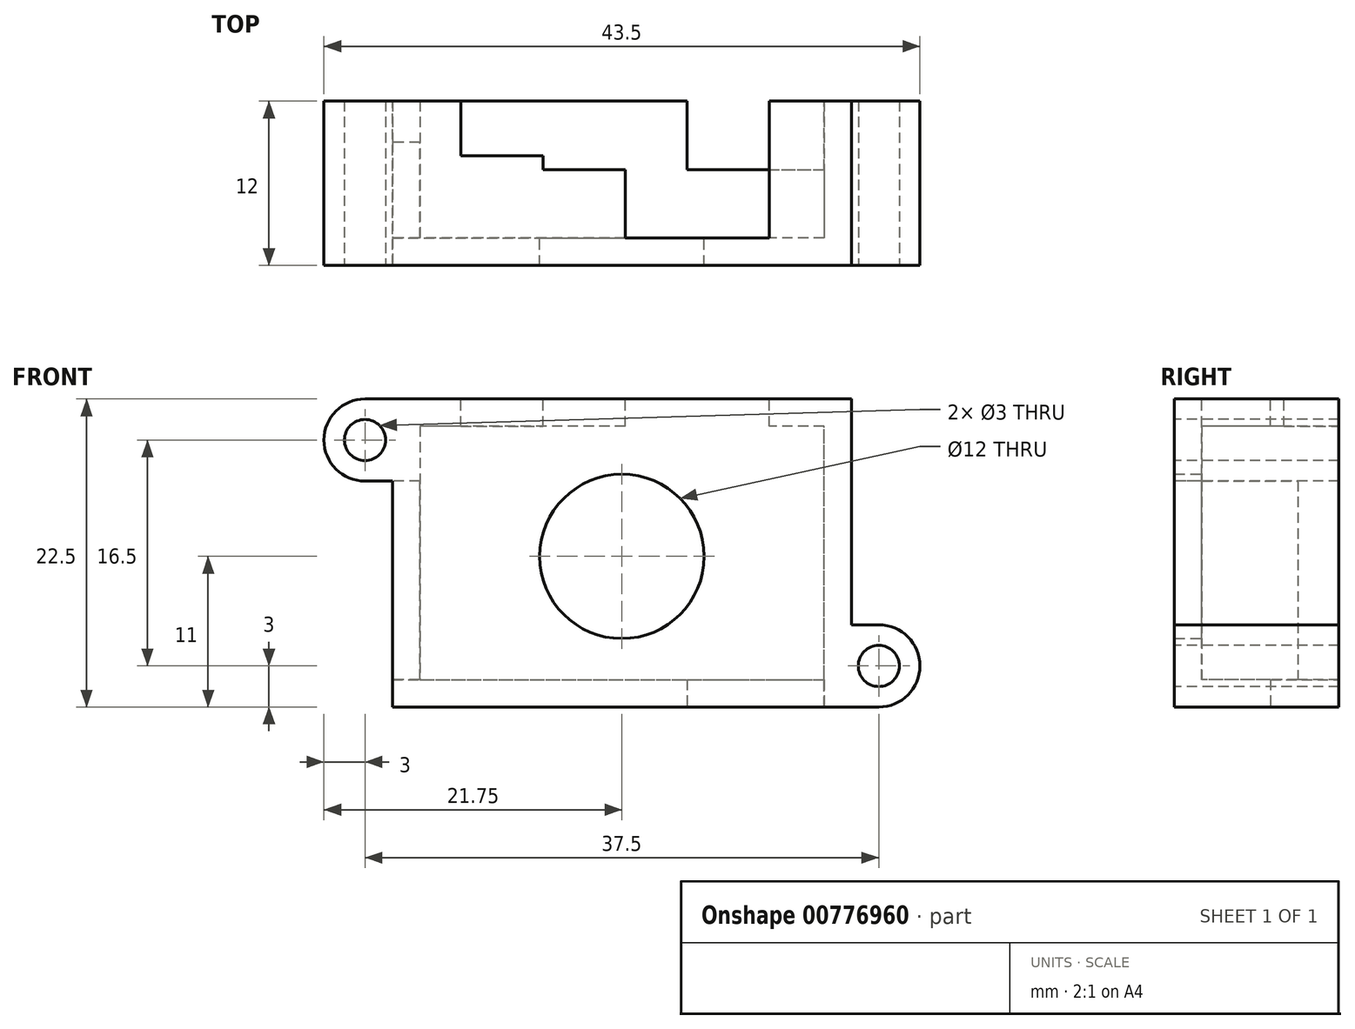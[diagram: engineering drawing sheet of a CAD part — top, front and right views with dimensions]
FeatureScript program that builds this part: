
annotation { "Feature Type Name" : "Feature", "Feature Type Description" : "" }
export const myFeature = defineFeature(function(context is Context, id is Id, definition is map)
    precondition{}
    {
        {
            var Q0;
            Q0=qCreatedBy(makeId("Front.planeOp"),FACE);
            var sketch = newSketch(context, id + "F0", { "sketchPlane" : qUnion([Q0])});
            skLineSegment(sketch, "E0.bottom", {"start": v(0, 0) * mm, "end": v(33.5, 0) * mm});
            skLineSegment(sketch, "E0.top", {"start": v(0, 22.5) * mm, "end": v(33.5, 22.5) * mm});
            skLineSegment(sketch, "E0.left", {"start": v(0, 0) * mm, "end": v(0, 22.5) * mm});
            skLineSegment(sketch, "E0.right", {"start": v(33.5, 0) * mm, "end": v(33.5, 22.5) * mm});
            skCircle(sketch, "E1", {"center": v(16.75, 11) * mm, "radius": 6 * mm});
            skSolve(sketch);
        }
        {
            var Q0;
            Q0=qSketchRegion(id+"F0",true);
            extrude(context, id + "F1", {"entities" : qUnion([Q0]), "depth" : 2 * mm, "offsetDistance" : 25 * mm});
        }
        {
            var Q0;
            Q0=makeQuery(id+"F1.opExtrude","CAP_FACE",FACE,{"disambiguationData":[OSD([sQuery(id+"F0.wireOp",EDGE,"E0.bottom"),sQuery(id+"F0.wireOp",EDGE,"E0.top"),sQuery(id+"F0.wireOp",EDGE,"E0.left"),sQuery(id+"F0.wireOp",EDGE,"E0.right"),sQuery(id+"F0.wireOp",EDGE,"E1")])],"isStart":true});
            var sketch = newSketch(context, id + "F2", { "sketchPlane" : qUnion([Q0])});
            skLineSegment(sketch, "E2", {"start": v(-33.5, 22.5) * mm, "end": v(-33.5, 0) * mm});
            skLineSegment(sketch, "E3", {"start": v(-33.5, 0) * mm, "end": v(0, 0) * mm});
            skLineSegment(sketch, "E4", {"start": v(0, 0) * mm, "end": v(0, 22.5) * mm});
            skLineSegment(sketch, "E5", {"start": v(0, 22.5) * mm, "end": v(-11, 22.5) * mm});
            skLineSegment(sketch, "E6", {"start": v(-11, 22.5) * mm, "end": v(-11, 20.5) * mm});
            skLineSegment(sketch, "E7", {"start": v(-11, 20.5) * mm, "end": v(-2, 20.5) * mm});
            skLineSegment(sketch, "E8", {"start": v(-2, 20.5) * mm, "end": v(-2, 2) * mm});
            skLineSegment(sketch, "E9", {"start": v(-2, 2) * mm, "end": v(-31.5, 2) * mm});
            skLineSegment(sketch, "E10", {"start": v(-31.5, 2) * mm, "end": v(-31.5, 20.5) * mm});
            skLineSegment(sketch, "E11", {"start": v(-31.5, 20.5) * mm, "end": v(-27.5, 20.5) * mm});
            skLineSegment(sketch, "E12", {"start": v(-27.5, 20.5) * mm, "end": v(-27.5, 22.5) * mm});
            skLineSegment(sketch, "E13", {"start": v(-27.5, 22.5) * mm, "end": v(-33.5, 22.5) * mm});
            skSolve(sketch);
        }
        {
            var Q0;
            Q0=qSketchRegion(id+"F2",true);
            extrude(context, id + "F3", {"entities" : qUnion([Q0]), "operationType" : NewBodyOperationType.ADD, "depth" : 10 * mm, "offsetDistance" : 25 * mm});
        }
        {
            var Q0;
            Q0=makeQuery(id+"F3.boolean.opBoolean","MERGE",FACE,{"derivedFrom":[makeQuery(id+"F1.opExtrude","SWEPT_FACE",FACE,{"disambiguationData":[OSD([sQuery(id+"F0.wireOp",EDGE,"E0.top")])]}),makeQuery(id+"F3.opExtrude","SWEPT_FACE",FACE,{"disambiguationData":[OSD([sQuery(id+"F2.wireOp",EDGE,"E5")])]}),makeQuery(id+"F3.opExtrude","SWEPT_FACE",FACE,{"disambiguationData":[OSD([sQuery(id+"F2.wireOp",EDGE,"E13")])]})]});
            var sketch = newSketch(context, id + "F4", { "sketchPlane" : qUnion([Q0])});
            skLineSegment(sketch, "E14.bottom", {"start": v(11, 10) * mm, "end": v(5, 10) * mm});
            skLineSegment(sketch, "E14.top", {"start": v(11, 6) * mm, "end": v(5, 6) * mm});
            skLineSegment(sketch, "E14.left", {"start": v(11, 10) * mm, "end": v(11, 6) * mm});
            skLineSegment(sketch, "E14.right", {"start": v(5, 10) * mm, "end": v(5, 6) * mm});
            skSolve(sketch);
        }
        {
            var Q0;
            Q0=qSketchRegion(id+"F4",true);
            var Q1;
            Q1=makeQuery(id+"F3.opExtrude","SWEPT_FACE",FACE,{"disambiguationData":[OSD([sQuery(id+"F2.wireOp",EDGE,"E7")])]});
            extrude(context, id + "F5", {"entities" : qUnion([Q0]), "operationType" : NewBodyOperationType.REMOVE, "endBound" : BoundingType.UP_TO_SURFACE, "oppositeDirection" : true, "depth" : 25 * mm, "endBoundEntityFace" : qUnion([Q1]), "offsetDistance" : 25 * mm});
        }
        {
            var Q0;
            Q0=makeQuery(id+"F1.opExtrude","CAP_FACE",FACE,{"disambiguationData":[OSD([sQuery(id+"F0.wireOp",EDGE,"E0.bottom"),sQuery(id+"F0.wireOp",EDGE,"E0.top"),sQuery(id+"F0.wireOp",EDGE,"E0.left"),sQuery(id+"F0.wireOp",EDGE,"E0.right"),sQuery(id+"F0.wireOp",EDGE,"E1")])],"isStart":false});
            var sketch = newSketch(context, id + "F6", { "sketchPlane" : qUnion([Q0])});
            skLineSegment(sketch, "E15.bottom", {"start": v(33.5, 0) * mm, "end": v(35.5, 0) * mm});
            skLineSegment(sketch, "E15.top", {"start": v(33.5, 6) * mm, "end": v(35.5, 6) * mm});
            skLineSegment(sketch, "E15.left", {"start": v(33.5, 0) * mm, "end": v(33.5, 6) * mm});
            skLineSegment(sketch, "E15.right", {"start": v(35.5, 0) * mm, "end": v(35.5, 6) * mm});
            skArc(sketch, "E16", {"start": v(35.5, 0) * mm, "mid": v(38.5, 3) * mm, "end": v(35.5, 6) * mm});
            skLineSegment(sketch, "E17.bottom", {"start": v(0, 22.5) * mm, "end": v(-2, 22.5) * mm});
            skLineSegment(sketch, "E17.top", {"start": v(0, 16.5) * mm, "end": v(-2, 16.5) * mm});
            skLineSegment(sketch, "E17.left", {"start": v(0, 22.5) * mm, "end": v(0, 16.5) * mm});
            skLineSegment(sketch, "E17.right", {"start": v(-2, 22.5) * mm, "end": v(-2, 16.5) * mm});
            skArc(sketch, "E18", {"start": v(-2, 22.5) * mm, "mid": v(-5, 19.5) * mm, "end": v(-2, 16.5) * mm});
            skCircle(sketch, "E19", {"center": v(35.5, 3) * mm, "radius": 1.5 * mm});
            skCircle(sketch, "E20", {"center": v(-2, 19.5) * mm, "radius": 1.5 * mm});
            skSolve(sketch);
        }
        {
            var Q0;
            Q0=qSketchRegion(id+"F6",true);
            var Q1;
            Q1=makeQuery(id+"F3.opExtrude","CAP_FACE",FACE,{"disambiguationData":[OSD([sQuery(id+"F2.wireOp",EDGE,"E2"),sQuery(id+"F2.wireOp",EDGE,"E3"),sQuery(id+"F2.wireOp",EDGE,"E4"),sQuery(id+"F2.wireOp",EDGE,"E5"),sQuery(id+"F2.wireOp",EDGE,"E6"),sQuery(id+"F2.wireOp",EDGE,"E7"),sQuery(id+"F2.wireOp",EDGE,"E8"),sQuery(id+"F2.wireOp",EDGE,"E9"),sQuery(id+"F2.wireOp",EDGE,"E10"),sQuery(id+"F2.wireOp",EDGE,"E11"),sQuery(id+"F2.wireOp",EDGE,"E12"),sQuery(id+"F2.wireOp",EDGE,"E13")])],"isStart":false});
            extrude(context, id + "F7", {"entities" : qUnion([Q0]), "operationType" : NewBodyOperationType.ADD, "endBound" : BoundingType.UP_TO_SURFACE, "oppositeDirection" : true, "depth" : 25 * mm, "endBoundEntityFace" : qUnion([Q1]), "offsetDistance" : 25 * mm});
        }
        {
            var Q0;
            Q0=makeQuery(id+"F7.boolean.opBoolean","MERGE",FACE,{"derivedFrom":[makeQuery(id+"F3.boolean.opBoolean","MERGE",FACE,{"derivedFrom":[makeQuery(id+"F1.opExtrude","SWEPT_FACE",FACE,{"disambiguationData":[OSD([sQuery(id+"F0.wireOp",EDGE,"E0.top")])]}),makeQuery(id+"F3.opExtrude","SWEPT_FACE",FACE,{"disambiguationData":[OSD([sQuery(id+"F2.wireOp",EDGE,"E5")])]}),makeQuery(id+"F3.opExtrude","SWEPT_FACE",FACE,{"disambiguationData":[OSD([sQuery(id+"F2.wireOp",EDGE,"E13")])]})]}),makeQuery(id+"F7.opExtrude","SWEPT_FACE",FACE,{"disambiguationData":[OSD([sQuery(id+"F6.wireOp",EDGE,"E17.bottom")])]})]});
            var sketch = newSketch(context, id + "F8", { "sketchPlane" : qUnion([Q0])});
            skLineSegment(sketch, "E21.bottom", {"start": v(11, 0) * mm, "end": v(17, 0) * mm});
            skLineSegment(sketch, "E21.top", {"start": v(11, 5) * mm, "end": v(17, 5) * mm});
            skLineSegment(sketch, "E21.left", {"start": v(11, 0) * mm, "end": v(11, 5) * mm});
            skLineSegment(sketch, "E21.right", {"start": v(17, 0) * mm, "end": v(17, 5) * mm});
            skSolve(sketch);
        }
        {
            var Q0;
            Q0=qSketchRegion(id+"F8",true);
            var Q1;
            Q1=makeQuery(id+"F3.opExtrude","SWEPT_FACE",FACE,{"disambiguationData":[OSD([sQuery(id+"F2.wireOp",EDGE,"E7")])]});
            extrude(context, id + "F9", {"entities" : qUnion([Q0]), "operationType" : NewBodyOperationType.ADD, "endBound" : BoundingType.UP_TO_SURFACE, "oppositeDirection" : true, "depth" : 25 * mm, "endBoundEntityFace" : qUnion([Q1]), "offsetDistance" : 25 * mm});
        }
        {
            var Q0;
            {var subQ0=sQuery(id+"F2.wireOp",EDGE,"E13");var subQ1=sQuery(id+"F2.wireOp",EDGE,"E12");var subQ2=sQuery(id+"F2.wireOp",EDGE,"E11");var subQ3=sQuery(id+"F2.wireOp",EDGE,"E10");var subQ4=sQuery(id+"F2.wireOp",EDGE,"E9");var subQ5=sQuery(id+"F2.wireOp",EDGE,"E8");var subQ6=sQuery(id+"F2.wireOp",EDGE,"E7");var subQ7=sQuery(id+"F2.wireOp",EDGE,"E6");var subQ8=sQuery(id+"F2.wireOp",EDGE,"E5");var subQ9=sQuery(id+"F2.wireOp",EDGE,"E4");var subQ10=sQuery(id+"F2.wireOp",EDGE,"E3");var subQ11=sQuery(id+"F2.wireOp",EDGE,"E2");Q0=makeQuery(id+"F7.boolean.opBoolean","MERGE",FACE,{"derivedFrom":[makeQuery(id+"F3.opExtrude","CAP_FACE",FACE,{"disambiguationData":[OSD([subQ11,subQ10,subQ9,subQ8,subQ7,subQ6,subQ5,subQ4,subQ3,subQ2,subQ1,subQ0])],"isStart":false}),makeQuery(id+"F7.opExtrude","CAP_FACE",FACE,{"disambiguationData":[OSD([subQ11,subQ10,subQ9,subQ8,subQ7,subQ6,subQ5,subQ4,subQ3,subQ2,subQ1,subQ0]),OD(0.0)],"isStart":false}),makeQuery(id+"F7.opExtrude","CAP_FACE",FACE,{"disambiguationData":[OSD([subQ11,subQ10,subQ9,subQ8,subQ7,subQ6,subQ5,subQ4,subQ3,subQ2,subQ1,subQ0]),OD(1.0)],"isStart":false})]});}
            var sketch = newSketch(context, id + "F10", { "sketchPlane" : qUnion([Q0])});
            skLineSegment(sketch, "E22.bottom", {"start": v(-31.5, 2) * mm, "end": v(-21.5, 2) * mm});
            skLineSegment(sketch, "E22.top", {"start": v(-31.5, 0) * mm, "end": v(-21.5, 0) * mm});
            skLineSegment(sketch, "E22.left", {"start": v(-31.5, 2) * mm, "end": v(-31.5, 0) * mm});
            skLineSegment(sketch, "E22.right", {"start": v(-21.5, 2) * mm, "end": v(-21.5, 0) * mm});
            skSolve(sketch);
        }
        {
            var Q0;
            Q0=qSketchRegion(id+"F10",true);
            extrude(context, id + "F11", {"entities" : qUnion([Q0]), "operationType" : NewBodyOperationType.REMOVE, "oppositeDirection" : true, "depth" : 5 * mm, "offsetDistance" : 25 * mm});
        }
        {
            var Q0;
            Q0=makeQuery(id+"F3.boolean.opBoolean","MERGE",FACE,{"derivedFrom":[makeQuery(id+"F1.opExtrude","SWEPT_FACE",FACE,{"disambiguationData":[OSD([sQuery(id+"F0.wireOp",EDGE,"E0.left")])]}),makeQuery(id+"F3.opExtrude","SWEPT_FACE",FACE,{"disambiguationData":[OSD([sQuery(id+"F2.wireOp",EDGE,"E4")])]})]});
            var sketch = newSketch(context, id + "F12", { "sketchPlane" : qUnion([Q0])});
            skLineSegment(sketch, "E23.bottom", {"start": v(-7, 16.5) * mm, "end": v(0, 16.5) * mm});
            skLineSegment(sketch, "E23.top", {"start": v(-7, 2) * mm, "end": v(0, 2) * mm});
            skLineSegment(sketch, "E23.left", {"start": v(-7, 16.5) * mm, "end": v(-7, 2) * mm});
            skLineSegment(sketch, "E23.right", {"start": v(0, 16.5) * mm, "end": v(0, 2) * mm});
            skSolve(sketch);
        }
        {
            var Q0;
            Q0 = qSketchRegion(id + "F12", true);
            extrude(context, id + "F13", {"entities" : qUnion([Q0]), "operationType" : NewBodyOperationType.REMOVE, "endBound" : BoundingType.UP_TO_NEXT, "oppositeDirection" : true, "depth" : 25 * mm, "offsetDistance" : 25 * mm});
        }
    });
